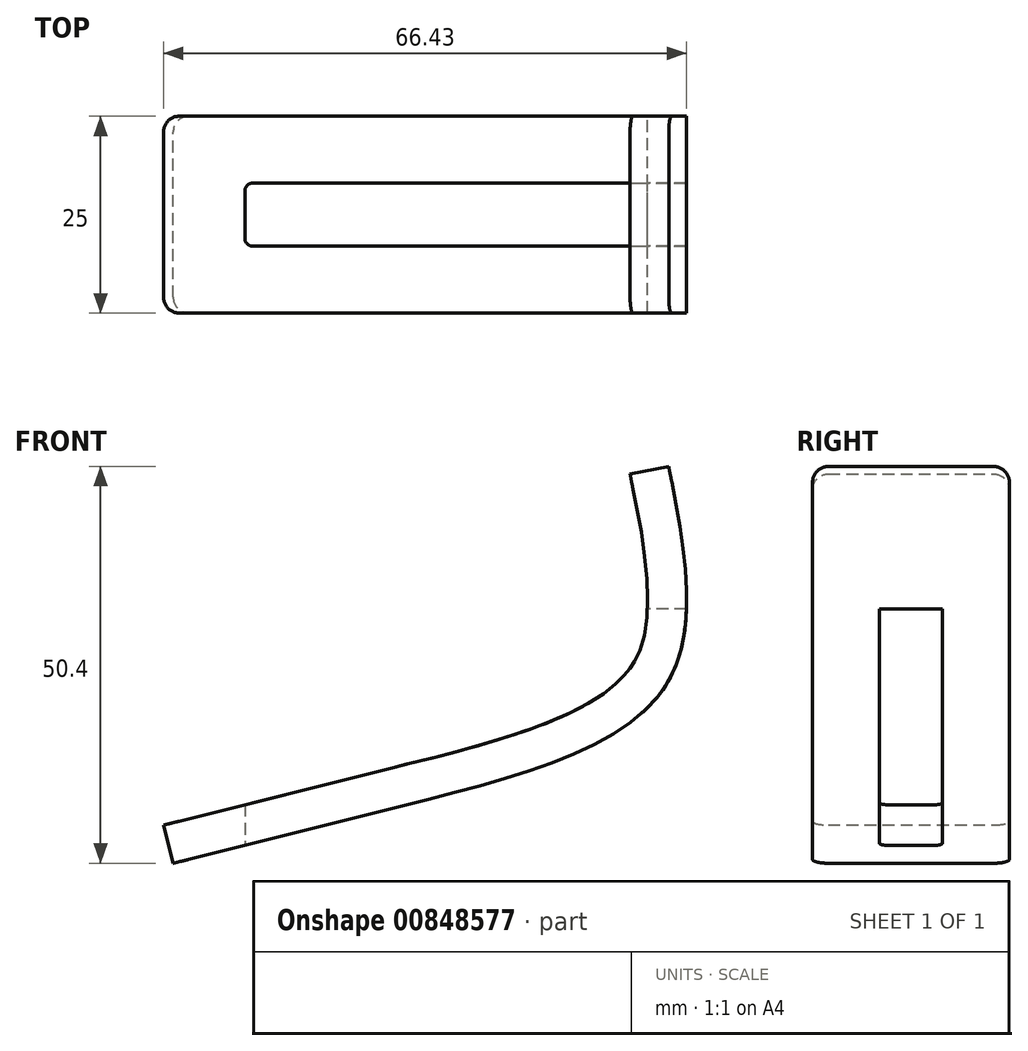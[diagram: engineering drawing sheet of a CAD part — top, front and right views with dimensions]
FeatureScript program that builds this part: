
annotation { "Feature Type Name" : "Feature", "Feature Type Description" : "" }
export const myFeature = defineFeature(function(context is Context, id is Id, definition is map)
    precondition{}
    {
        {
            var Q0;
            Q0=qCreatedBy(makeId("Front.planeOp"),FACE);
            var sketch = newSketch(context, id + "F0", { "sketchPlane" : qUnion([Q0])});
            skFitSpline(sketch, "E0", {"points": [v(0, 0) * mm, v(33.3, 15.04) * mm, v(33.84, 43.1) * mm], "startDerivative": vector(78.84, 19.74) * mm, "endDerivative": vector(-13.18, 67.52) * mm});
            skFitSpline(sketch, "E1.0", {"points": [v(-1.21, 4.85) * mm, v(2.07, 5.67) * mm, v(6.94, 6.9) * mm, v(12.96, 8.65) * mm, v(17.14, 10.07) * mm, v(20.88, 11.6) * mm, v(24.09, 13.26) * mm, v(26.22, 14.73) * mm, v(27.59, 15.93) * mm, v(28.3, 16.68) * mm, v(28.78, 17.3) * mm, v(29.1, 17.75) * mm, v(29.4, 18.2) * mm, v(29.93, 19.18) * mm, v(30.55, 20.82) * mm, v(31.04, 23.5) * mm, v(31.17, 26.63) * mm, v(30.95, 30.14) * mm, v(30.29, 35.2) * mm, v(29.48, 39.34) * mm, v(28.93, 42.15) * mm]});
            skLineSegment(sketch, "E2", {"start": v(33.84, 43.1) * mm, "end": v(28.93, 42.15) * mm});
            skLineSegment(sketch, "E3", {"start": v(-1.21, 4.85) * mm, "end": v(0, 0) * mm});
            skLineSegment(sketch, "E4", {"start": v(-1.21, 4.85) * mm, "end": v(-30.32, -2.44) * mm});
            skLineSegment(sketch, "E5", {"start": v(-30.32, -2.44) * mm, "end": v(-29.1, -7.29) * mm});
            skLineSegment(sketch, "E6", {"start": v(-29.1, -7.29) * mm, "end": v(0, 0) * mm});
            skSolve(sketch);
        }
        {
            var Q0;
            Q0=makeQuery(id+"F0.imprint","IMPRINT",FACE,{"disambiguationData":[TD([[makeQuery(id+"F0.imprint","IMPRINT",EDGE,{"derivedFrom":sQuery(id+"F0.wireOp",EDGE,"E0")}),1.0]])]});
            var Q1;
            Q1=makeQuery(id+"F0.imprint","IMPRINT",FACE,{"disambiguationData":[TD([[makeQuery(id+"F0.imprint","IMPRINT",EDGE,{"derivedFrom":sQuery(id+"F0.wireOp",EDGE,"E3")}),-1.0]])]});
            extrude(context, id + "F1", {"entities" : qUnion([Q0, Q1]), "depth" : 12.5 * mm, "offsetDistance" : 25 * mm, "hasSecondDirection" : true, "secondDirectionOppositeDirection" : true, "secondDirectionDepth" : 12.5 * mm});
        }
        {
            var Q0;
            Q0=makeQuery(id+"F1.opExtrude","CAP_EDGE",EDGE,{"disambiguationData":[OSD([sQuery(id+"F0.wireOp",EDGE,"E2")])],"isStart":false});
            var Q1;
            Q1=makeQuery(id+"F1.opExtrude","CAP_EDGE",EDGE,{"disambiguationData":[OSD([sQuery(id+"F0.wireOp",EDGE,"E2")])],"isStart":true});
            var Q2;
            Q2=makeQuery(id+"F1.opExtrude","CAP_EDGE",EDGE,{"disambiguationData":[OSD([sQuery(id+"F0.wireOp",EDGE,"E5")])],"isStart":false});
            var Q3;
            Q3=makeQuery(id+"F1.opExtrude","CAP_EDGE",EDGE,{"disambiguationData":[OSD([sQuery(id+"F0.wireOp",EDGE,"E5")])],"isStart":true});
            fillet(context, id + "F2", {"entities" : qUnion([Q0, Q1, Q2, Q3]), "radius" : 2 * mm, "tangentPropagation" : true, "allowEdgeOverflow" : false});
        }
        {
            var Q0;
            Q0=qCreatedBy(makeId("Top.planeOp"),FACE);
            var sketch = newSketch(context, id + "F3", { "sketchPlane" : qUnion([Q0])});
            skLineSegment(sketch, "E7", {"start": v(0, 0) * mm, "end": v(15, 0) * mm, "construction": true});
            skLineSegment(sketch, "E8.bottom", {"start": v(50, -4) * mm, "end": v(-19, -4) * mm});
            skLineSegment(sketch, "E8.top", {"start": v(50, 4) * mm, "end": v(-19, 4) * mm});
            skLineSegment(sketch, "E8.left", {"start": v(50, -4) * mm, "end": v(50, 4) * mm});
            skLineSegment(sketch, "E8.right", {"start": v(-20, -3) * mm, "end": v(-20, 3) * mm});
            skPoint(sketch, "E8.middle", {"position": v(15, 0) * mm});
            skPoint(sketch, "E9.visualSharp", {"position": v(-20, -4) * mm});
            skArc(sketch, "E9.filletArc", {"start": v(-20, -3) * mm, "mid": v(-19.7, -3.7) * mm, "end": v(-19, -4) * mm});
            skPoint(sketch, "E10.visualSharp", {"position": v(-20, 4) * mm});
            skArc(sketch, "E10.filletArc", {"start": v(-19, 4) * mm, "mid": v(-19.7, 3.7) * mm, "end": v(-20, 3) * mm});
            skSolve(sketch);
        }
        {
            var Q0;
            Q0=makeQuery(id+"F3.imprint","IMPRINT",FACE,{"disambiguationData":[TD([[makeQuery(id+"F3.imprint","IMPRINT",EDGE,{"derivedFrom":sQuery(id+"F3.wireOp",EDGE,"E8.bottom")}),-1.0]])]});
            extrude(context, id + "F4", {"entities" : qUnion([Q0]), "operationType" : NewBodyOperationType.REMOVE, "depth" : 25 * mm, "offsetDistance" : 25 * mm, "hasSecondDirection" : true, "secondDirectionOppositeDirection" : true, "secondDirectionDepth" : 25 * mm});
        }
    });
